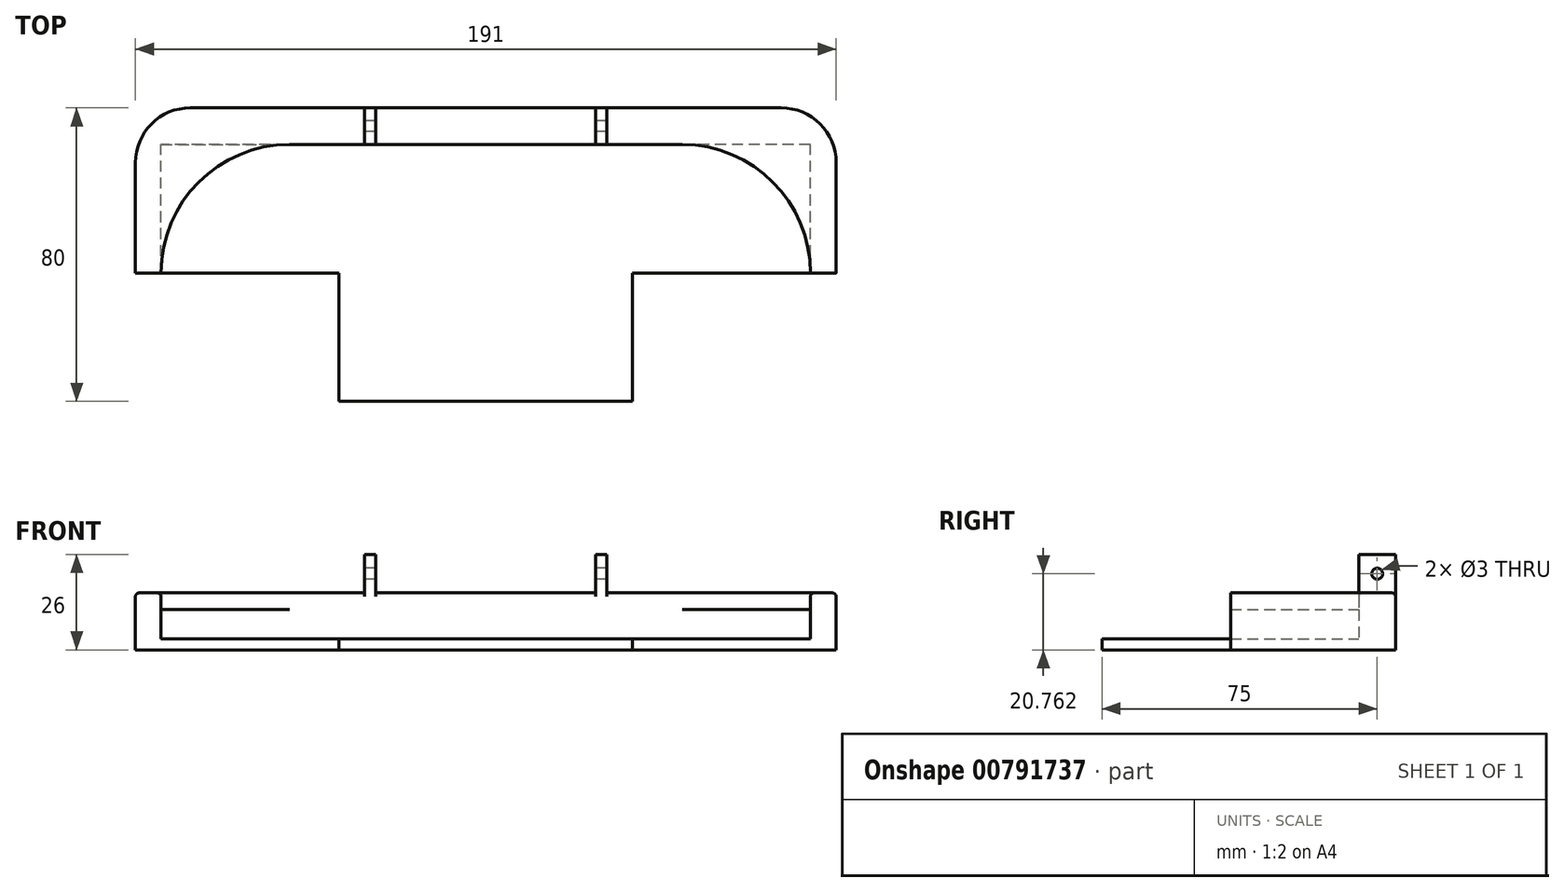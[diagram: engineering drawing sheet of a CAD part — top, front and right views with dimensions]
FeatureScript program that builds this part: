
annotation { "Feature Type Name" : "Feature", "Feature Type Description" : "" }
export const myFeature = defineFeature(function(context is Context, id is Id, definition is map)
    precondition{}
    {
        {
            var Q0;
            Q0=qCreatedBy(makeId("Top.planeOp"),FACE);
            var sketch = newSketch(context, id + "F0", { "sketchPlane" : qUnion([Q0])});
            skLineSegment(sketch, "E0", {"start": v(-95.5, 0) * mm, "end": v(-95.5, 30) * mm});
            skLineSegment(sketch, "E1", {"start": v(-80.5, 45) * mm, "end": v(80.5, 45) * mm});
            skLineSegment(sketch, "E2", {"start": v(95.5, 30) * mm, "end": v(95.5, 0) * mm});
            skLineSegment(sketch, "E3", {"start": v(95.5, 0) * mm, "end": v(88.5, 0) * mm});
            skLineSegment(sketch, "E4", {"start": v(88.5, 0) * mm, "end": v(88.5, 0) * mm});
            skLineSegment(sketch, "E5", {"start": v(53.5, 35) * mm, "end": v(-53.5, 35) * mm});
            skLineSegment(sketch, "E6", {"start": v(-88.5, 0) * mm, "end": v(-88.5, 0) * mm});
            skLineSegment(sketch, "E7", {"start": v(-88.5, 0) * mm, "end": v(-95.5, 0) * mm});
            skLineSegment(sketch, "E8", {"start": v(0, 0) * mm, "end": v(0, 35) * mm, "construction": true});
            skLineSegment(sketch, "E9", {"start": v(-88.5, 0) * mm, "end": v(88.5, 0) * mm});
            skPoint(sketch, "E10.visualSharp", {"position": v(-88.5, 35) * mm});
            skArc(sketch, "E10.filletArc", {"start": v(-53.5, 35) * mm, "mid": v(-78.25, 24.75) * mm, "end": v(-88.5, 0) * mm});
            skPoint(sketch, "E11.visualSharp", {"position": v(88.5, 35) * mm});
            skArc(sketch, "E11.filletArc", {"start": v(88.5, 0) * mm, "mid": v(78.25, 24.75) * mm, "end": v(53.5, 35) * mm});
            skLineSegment(sketch, "E12", {"start": v(-88.5, 0) * mm, "end": v(-88.5, 35) * mm});
            skLineSegment(sketch, "E13", {"start": v(-88.5, 35) * mm, "end": v(-53.5, 35) * mm});
            skLineSegment(sketch, "E14", {"start": v(88.5, 0) * mm, "end": v(88.5, 35) * mm});
            skLineSegment(sketch, "E15", {"start": v(88.5, 35) * mm, "end": v(53.5, 35) * mm});
            skLineSegment(sketch, "E16", {"start": v(-30, 45) * mm, "end": v(30, 45) * mm, "construction": true});
            skLineSegment(sketch, "E17", {"start": v(0, 35) * mm, "end": v(0, 45) * mm, "construction": true});
            skLineSegment(sketch, "E18.bottom", {"start": v(-30, 45) * mm, "end": v(-33, 45) * mm});
            skLineSegment(sketch, "E18.top", {"start": v(-30, 35) * mm, "end": v(-33, 35) * mm});
            skLineSegment(sketch, "E18.left", {"start": v(-30, 45) * mm, "end": v(-30, 35) * mm});
            skLineSegment(sketch, "E18.right", {"start": v(-33, 45) * mm, "end": v(-33, 35) * mm});
            skLineSegment(sketch, "E19.bottom", {"start": v(30, 45) * mm, "end": v(33, 45) * mm});
            skLineSegment(sketch, "E19.top", {"start": v(30, 35) * mm, "end": v(33, 35) * mm});
            skLineSegment(sketch, "E19.left", {"start": v(30, 45) * mm, "end": v(30, 35) * mm});
            skLineSegment(sketch, "E19.right", {"start": v(33, 45) * mm, "end": v(33, 35) * mm});
            skLineSegment(sketch, "E20.bottom", {"start": v(-40, 0) * mm, "end": v(40, 0) * mm});
            skLineSegment(sketch, "E20.top", {"start": v(-40, -35) * mm, "end": v(40, -35) * mm});
            skLineSegment(sketch, "E20.left", {"start": v(-40, 0) * mm, "end": v(-40, -35) * mm});
            skLineSegment(sketch, "E20.right", {"start": v(40, 0) * mm, "end": v(40, -35) * mm});
            skPoint(sketch, "E21.visualSharp", {"position": v(-95.5, 45) * mm});
            skArc(sketch, "E21.filletArc", {"start": v(-80.5, 45) * mm, "mid": v(-91.1, 40.6) * mm, "end": v(-95.5, 30) * mm});
            skPoint(sketch, "E22.visualSharp", {"position": v(95.5, 45) * mm});
            skArc(sketch, "E22.filletArc", {"start": v(95.5, 30) * mm, "mid": v(91.1, 40.6) * mm, "end": v(80.5, 45) * mm});
            skSolve(sketch);
        }
        {
            var Q0;
            {var subQ0=sQuery(id+"F0.wireOp",EDGE,"E19.left");var subQ7=sQuery(id+"F0.wireOp",EDGE,"E11.filletArc");var subQ12=sQuery(id+"F0.wireOp",EDGE,"E10.filletArc");var subQ14=sQuery(id+"F0.wireOp",EDGE,"E18.left");var subQ28=makeQuery(id+"F0.imprint","IMPRINT",EDGE,{"derivedFrom":subQ12});var subQ29=makeQuery(id+"F0.imprint","IMPRINT",EDGE,{"derivedFrom":subQ7});var subQ33=makeQuery(id+"F0.imprint","IMPRINT",EDGE,{"derivedFrom":subQ0});var subQ38=makeQuery(id+"F0.imprint","IMPRINT",EDGE,{"derivedFrom":subQ14});Q0=qUnion([makeQuery(id+"F0.imprint","IMPRINT",FACE,{"disambiguationData":[TD([[makeQuery(id+"F0.imprint","IMPRINT",EDGE,{"derivedFrom":sQuery(id+"F0.wireOp",EDGE,"E20.top")}),1.0]])]}),makeQuery(id+"F0.imprint","IMPRINT",FACE,{"disambiguationData":[TD([[subQ28,-1.0]])]}),makeQuery(id+"F0.imprint","IMPRINT",FACE,{"disambiguationData":[TD([[subQ29,-1.0]])]}),makeQuery(id+"F0.imprint","IMPRINT",FACE,{"disambiguationData":[TD([[makeQuery(id+"F0.imprint","IMPRINT",EDGE,{"derivedFrom":sQuery(id+"F0.wireOp",EDGE,"E0")}),-1.0]])]}),makeQuery(id+"F0.imprint","IMPRINT",FACE,{"disambiguationData":[TD([[subQ38,1.0]])]}),makeQuery(id+"F0.imprint","IMPRINT",FACE,{"disambiguationData":[TD([[makeQuery(id+"F0.imprint","IMPRINT",EDGE,{"derivedFrom":sQuery(id+"F0.wireOp",EDGE,"E2")}),-1.0]])]}),makeQuery(id+"F0.imprint","IMPRINT",FACE,{"disambiguationData":[TD([[subQ38,-1.0]])]}),makeQuery(id+"F0.imprint","IMPRINT",FACE,{"disambiguationData":[TD([[subQ33,1.0]])]}),makeQuery(id+"F0.imprint","IMPRINT",FACE,{"disambiguationData":[TD([[subQ28,1.0]])]})]);}
            extrude(context, id + "F1", {"entities" : qUnion([Q0]), "oppositeDirection" : true, "depth" : 3 * mm, "offsetDistance" : 25 * mm});
        }
        {
            var Q0;
            Q0=makeQuery(id+"F0.imprint","IMPRINT",FACE,{"disambiguationData":[TD([[makeQuery(id+"F0.imprint","IMPRINT",EDGE,{"derivedFrom":sQuery(id+"F0.wireOp",EDGE,"E0")}),-1.0]])]});
            var Q1;
            {var subQ0=sQuery(id+"F0.wireOp",EDGE,"E18.left");Q1=makeQuery(id+"F0.imprint","IMPRINT",FACE,{"disambiguationData":[TD([[makeQuery(id+"F0.imprint","IMPRINT",EDGE,{"derivedFrom":subQ0}),-1.0]])]});}
            var Q2;
            {var subQ0=sQuery(id+"F0.wireOp",EDGE,"E18.left");Q2=makeQuery(id+"F0.imprint","IMPRINT",FACE,{"disambiguationData":[TD([[makeQuery(id+"F0.imprint","IMPRINT",EDGE,{"derivedFrom":subQ0}),1.0]])]});}
            var Q3;
            {var subQ2=sQuery(id+"F0.wireOp",EDGE,"E19.left");Q3=makeQuery(id+"F0.imprint","IMPRINT",FACE,{"disambiguationData":[TD([[makeQuery(id+"F0.imprint","IMPRINT",EDGE,{"derivedFrom":subQ2}),1.0]])]});}
            var Q4;
            Q4=makeQuery(id+"F0.imprint","IMPRINT",FACE,{"disambiguationData":[TD([[makeQuery(id+"F0.imprint","IMPRINT",EDGE,{"derivedFrom":sQuery(id+"F0.wireOp",EDGE,"E2")}),-1.0]])]});
            var Q5;
            Q5=makeQuery(id+"F0.imprint","IMPRINT",FACE,{"disambiguationData":[TD([[makeQuery(id+"F0.imprint","IMPRINT",EDGE,{"derivedFrom":sQuery(id+"F0.wireOp",EDGE,"E10.filletArc")}),-1.0]])]});
            var Q6;
            Q6=makeQuery(id+"F0.imprint","IMPRINT",FACE,{"disambiguationData":[TD([[makeQuery(id+"F0.imprint","IMPRINT",EDGE,{"derivedFrom":sQuery(id+"F0.wireOp",EDGE,"E11.filletArc")}),-1.0]])]});
            extrude(context, id + "F2", {"entities" : qUnion([Q0, Q1, Q2, Q3, Q4, Q5, Q6]), "operationType" : NewBodyOperationType.ADD, "depth" : 9.52 * mm + 3 * mm, "offsetDistance" : 25 * mm});
        }
        {
            var Q0;
            Q0=makeQuery(id+"F0.imprint","IMPRINT",FACE,{"disambiguationData":[TD([[makeQuery(id+"F0.imprint","IMPRINT",EDGE,{"derivedFrom":sQuery(id+"F0.wireOp",EDGE,"E10.filletArc")}),-1.0]])]});
            var Q1;
            Q1=makeQuery(id+"F0.imprint","IMPRINT",FACE,{"disambiguationData":[TD([[makeQuery(id+"F0.imprint","IMPRINT",EDGE,{"derivedFrom":sQuery(id+"F0.wireOp",EDGE,"E11.filletArc")}),-1.0]])]});
            extrude(context, id + "F3", {"entities" : qUnion([Q0, Q1]), "operationType" : NewBodyOperationType.REMOVE, "depth" : 10 * mm - 2.03 * mm, "offsetDistance" : 25 * mm});
        }
        {
            var Q0;
            {var subQ0=sQuery(id+"F0.wireOp",EDGE,"E18.left");Q0=makeQuery(id+"F0.imprint","IMPRINT",FACE,{"disambiguationData":[TD([[makeQuery(id+"F0.imprint","IMPRINT",EDGE,{"derivedFrom":subQ0}),-1.0]])]});}
            var Q1;
            {var subQ2=sQuery(id+"F0.wireOp",EDGE,"E19.left");Q1=makeQuery(id+"F0.imprint","IMPRINT",FACE,{"disambiguationData":[TD([[makeQuery(id+"F0.imprint","IMPRINT",EDGE,{"derivedFrom":subQ2}),1.0]])]});}
            extrude(context, id + "F4", {"entities" : qUnion([Q0, Q1]), "operationType" : NewBodyOperationType.ADD, "depth" : (13 + 10) * mm, "offsetDistance" : 25 * mm});
        }
        {
            var Q0;
            Q0=makeQuery(id+"F4.opExtrude","SWEPT_FACE",FACE,{"disambiguationData":[OSD([sQuery(id+"F0.wireOp",EDGE,"E18.right")])]});
            var sketch = newSketch(context, id + "F5", { "sketchPlane" : qUnion([Q0])});
            skCircle(sketch, "E23", {"center": v(-40, 17.76) * mm, "radius": 1.5 * mm});
            skLineSegment(sketch, "E24", {"start": v(-40, 23) * mm, "end": v(-40, 12.53) * mm, "construction": true});
            skSolve(sketch);
        }
        {
            var Q0;
            Q0 = qSketchRegion(id + "F5", true);
            extrude(context, id + "F6", {"entities" : qUnion([Q0]), "operationType" : NewBodyOperationType.REMOVE, "endBound" : BoundingType.THROUGH_ALL, "oppositeDirection" : true, "depth" : 25 * mm, "offsetDistance" : 25 * mm});
        }
        {
            var Q0;
            Q0=makeQuery(id+"F3.boolean.opBoolean","COPY",EDGE,{"derivedFrom":makeQuery(id+"F3.opExtrude","CAP_EDGE",EDGE,{"disambiguationData":[OSD([sQuery(id+"F0.wireOp",EDGE,"E10.filletArc")])],"isStart":false})});
            var Q1;
            Q1=makeQuery(id+"F3.boolean.opBoolean","COPY",EDGE,{"derivedFrom":makeQuery(id+"F3.opExtrude","CAP_EDGE",EDGE,{"disambiguationData":[OSD([sQuery(id+"F0.wireOp",EDGE,"E11.filletArc")])],"isStart":false})});
            var Q2;
            Q2=makeQuery(id+"F2.opExtrude","CAP_EDGE",EDGE,{"disambiguationData":[OSD([sQuery(id+"F0.wireOp",EDGE,"E10.filletArc")])],"isStart":false});
            var Q3;
            Q3=makeQuery(id+"F2.opExtrude","CAP_EDGE",EDGE,{"disambiguationData":[OSD([sQuery(id+"F0.wireOp",EDGE,"E11.filletArc")])],"isStart":false});
            var Q4;
            Q4=makeQuery(id+"F2.opExtrude","CAP_EDGE",EDGE,{"disambiguationData":[OSD([sQuery(id+"F0.wireOp",EDGE,"E22.filletArc")])],"isStart":false});
            var Q5;
            Q5=makeQuery(id+"F2.opExtrude","CAP_EDGE",EDGE,{"disambiguationData":[OSD([sQuery(id+"F0.wireOp",EDGE,"E21.filletArc")])],"isStart":false});
            var Q6;
            {var subQ0=sQuery(id+"F0.wireOp",EDGE,"E18.left");var subQ1=sQuery(id+"F0.wireOp",EDGE,"E1");Q6=makeQuery(id+"F4.boolean.opBoolean","SPLIT",EDGE,{"disambiguationData":[TD([makeQuery(id+"F4.opExtrude","SWEPT_FACE",FACE,{"disambiguationData":[OSD([subQ0])]})])],"derivedFrom":makeQuery(id+"F2.opExtrude","CAP_EDGE",EDGE,{"disambiguationData":[OSD([subQ1])],"isStart":false})});}
            var Q7;
            {var subQ1=sQuery(id+"F0.wireOp",EDGE,"E5");var subQ2=sQuery(id+"F0.wireOp",EDGE,"E18.left");Q7=makeQuery(id+"F4.boolean.opBoolean","SPLIT",EDGE,{"disambiguationData":[TD([makeQuery(id+"F4.opExtrude","SWEPT_FACE",FACE,{"disambiguationData":[OSD([subQ2])]})])],"derivedFrom":makeQuery(id+"F2.opExtrude","CAP_EDGE",EDGE,{"disambiguationData":[OSD([subQ1])],"isStart":false})});}
            fillet(context, id + "F7", {"entities" : qUnion([Q0, Q1, Q2, Q3, Q4, Q5, Q6, Q7]), "radius" : 1 * mm, "tangentPropagation" : true, "allowEdgeOverflow" : false});
        }
    });
